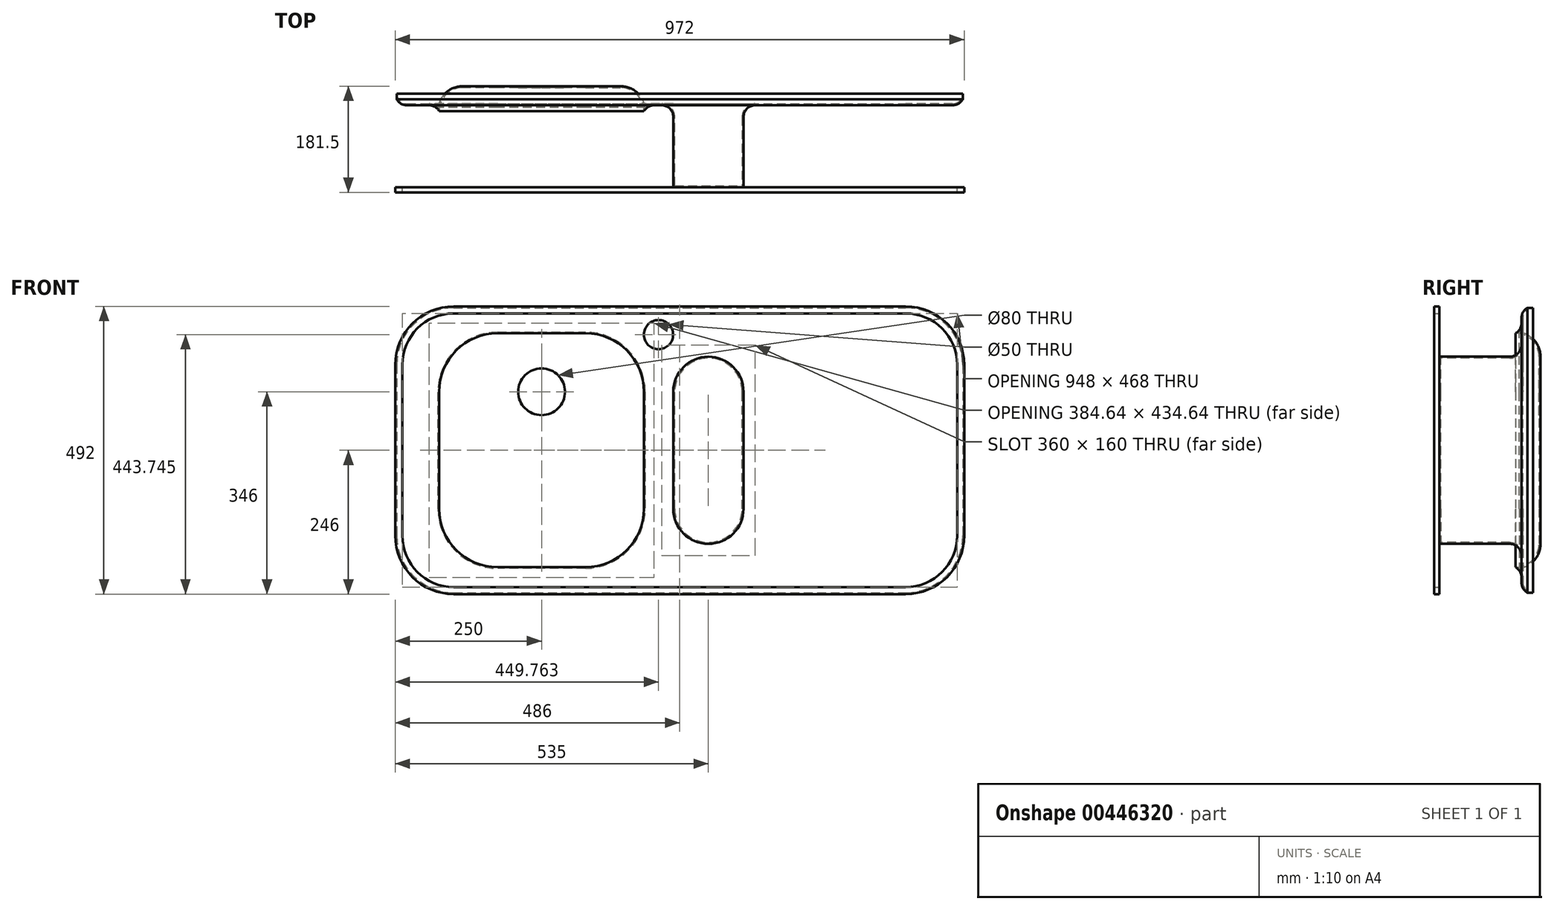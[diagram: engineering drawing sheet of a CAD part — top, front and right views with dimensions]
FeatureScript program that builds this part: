
annotation { "Feature Type Name" : "Feature", "Feature Type Description" : "" }
export const myFeature = defineFeature(function(context is Context, id is Id, definition is map)
    precondition{}
    {
        {
            var Q0;
            Q0=qCreatedBy(makeId("Front.planeOp"),FACE);
            var sketch = newSketch(context, id + "F0", { "sketchPlane" : qUnion([Q0])});
            skLineSegment(sketch, "E0.bottom", {"start": v(386, -246) * mm, "end": v(-386, -246) * mm});
            skLineSegment(sketch, "E0.top", {"start": v(386, 246) * mm, "end": v(-386, 246) * mm});
            skLineSegment(sketch, "E0.left", {"start": v(486, -146) * mm, "end": v(486, 146) * mm});
            skLineSegment(sketch, "E0.right", {"start": v(-486, -146) * mm, "end": v(-486, 146) * mm});
            skPoint(sketch, "E0.middle", {"position": v(0, 0) * mm});
            skPoint(sketch, "E1.visualSharp", {"position": v(486, -246) * mm});
            skArc(sketch, "E1.filletArc", {"start": v(386, -246) * mm, "mid": v(456.71, -216.71) * mm, "end": v(486, -146) * mm});
            skPoint(sketch, "E2.visualSharp", {"position": v(-486, -246) * mm});
            skArc(sketch, "E2.filletArc", {"start": v(-486, -146) * mm, "mid": v(-456.71, -216.71) * mm, "end": v(-386, -246) * mm});
            skPoint(sketch, "E3.visualSharp", {"position": v(-486, 246) * mm});
            skArc(sketch, "E3.filletArc", {"start": v(-386, 246) * mm, "mid": v(-456.71, 216.71) * mm, "end": v(-486, 146) * mm});
            skPoint(sketch, "E4.visualSharp", {"position": v(486, 246) * mm});
            skArc(sketch, "E4.filletArc", {"start": v(486, 146) * mm, "mid": v(456.71, 216.71) * mm, "end": v(386, 246) * mm});
            skSolve(sketch);
        }
        {
            var Q0;
            Q0 = qSketchRegion(id + "F0", true);
            extrude(context, id + "F1", {"entities" : qUnion([Q0]), "oppositeDirection" : true, "depth" : 300 * mm});
        }
        {
            var Q0;
            Q0=makeQuery(id+"F1.opExtrude","CAP_FACE",FACE,{"disambiguationData":[OSD([sQuery(id+"F0.wireOp",EDGE,"E0.bottom"),sQuery(id+"F0.wireOp",EDGE,"E0.top"),sQuery(id+"F0.wireOp",EDGE,"E0.left"),sQuery(id+"F0.wireOp",EDGE,"E0.right"),sQuery(id+"F0.wireOp",EDGE,"E1.filletArc"),sQuery(id+"F0.wireOp",EDGE,"E2.filletArc"),sQuery(id+"F0.wireOp",EDGE,"E3.filletArc"),sQuery(id+"F0.wireOp",EDGE,"E4.filletArc")])],"isStart":true});
            var sketch = newSketch(context, id + "F2", { "sketchPlane" : qUnion([Q0])});
            skLineSegment(sketch, "E5.bottom", {"start": v(-61, 200) * mm, "end": v(-411, 200) * mm});
            skLineSegment(sketch, "E5.top", {"start": v(-61, -200) * mm, "end": v(-411, -200) * mm});
            skLineSegment(sketch, "E5.left", {"start": v(-61, 200) * mm, "end": v(-61, -200) * mm});
            skLineSegment(sketch, "E5.right", {"start": v(-411, 200) * mm, "end": v(-411, -200) * mm});
            skPoint(sketch, "E5.middle", {"position": v(-236, 0) * mm});
            skSolve(sketch);
        }
        {
            var Q0;
            {var subQ5=sQuery(id+"F2.wireOp",EDGE,"E5.bottom");Q0=makeQuery(id+"F2.imprint","IMPRINT",FACE,{"disambiguationData":[TD([[makeQuery(id+"F2.imprint","IMPRINT",EDGE,{"derivedFrom":subQ5}),1.0]])]});}
            var Q1;
            {var subQ5=sQuery(id+"F2.wireOp",EDGE,"E5.top");Q1=makeQuery(id+"F2.imprint","IMPRINT",FACE,{"disambiguationData":[TD([[makeQuery(id+"F2.imprint","IMPRINT",EDGE,{"derivedFrom":subQ5}),-1.0]])]});}
            extrude(context, id + "F3", {"entities" : qUnion([Q0, Q1]), "operationType" : NewBodyOperationType.REMOVE, "oppositeDirection" : true, "depth" : 170 * mm});
        }
        {
            var Q0;
            Q0=makeQuery(id+"F3.boolean.opBoolean","COPY",FACE,{"derivedFrom":makeQuery(id+"F3.opExtrude","CAP_FACE",FACE,{"disambiguationData":[OSD([sQuery(id+"F2.wireOp",EDGE,"E5.bottom"),sQuery(id+"F2.wireOp",EDGE,"E5.top"),sQuery(id+"F2.wireOp",EDGE,"E5.left"),sQuery(id+"F2.wireOp",EDGE,"E5.right")])],"isStart":false})});
            fillet(context, id + "F4", {"entities" : qUnion([Q0]), "radius" : 40 * mm, "tangentPropagation" : true, "allowEdgeOverflow" : false});
        }
        {
            var Q0;
            Q0=makeQuery(id+"F3.boolean.opBoolean","COPY",EDGE,{"derivedFrom":makeQuery(id+"F3.opExtrude","SWEPT_EDGE",EDGE,{"disambiguationData":[OSD([sQuery(id+"F2.wireOp",EDGE,"E5.bottom"),sQuery(id+"F2.wireOp",EDGE,"E5.right")])]})});
            var Q1;
            Q1=makeQuery(id+"F3.boolean.opBoolean","COPY",EDGE,{"derivedFrom":makeQuery(id+"F3.opExtrude","SWEPT_EDGE",EDGE,{"disambiguationData":[OSD([sQuery(id+"F2.wireOp",EDGE,"E5.top"),sQuery(id+"F2.wireOp",EDGE,"E5.right")])]})});
            var Q2;
            Q2=makeQuery(id+"F3.boolean.opBoolean","COPY",EDGE,{"derivedFrom":makeQuery(id+"F3.opExtrude","SWEPT_EDGE",EDGE,{"disambiguationData":[OSD([sQuery(id+"F2.wireOp",EDGE,"E5.bottom"),sQuery(id+"F2.wireOp",EDGE,"E5.left")])]})});
            var Q3;
            Q3=makeQuery(id+"F3.boolean.opBoolean","COPY",EDGE,{"derivedFrom":makeQuery(id+"F3.opExtrude","SWEPT_EDGE",EDGE,{"disambiguationData":[OSD([sQuery(id+"F2.wireOp",EDGE,"E5.top"),sQuery(id+"F2.wireOp",EDGE,"E5.left")])]})});
            fillet(context, id + "F5", {"entities" : qUnion([Q0, Q1, Q2, Q3]), "radius" : 100 * mm, "tangentPropagation" : true, "allowEdgeOverflow" : false});
        }
        {
            var Q0;
            Q0=makeQuery(id+"F1.opExtrude","CAP_FACE",FACE,{"disambiguationData":[OSD([sQuery(id+"F0.wireOp",EDGE,"E0.bottom"),sQuery(id+"F0.wireOp",EDGE,"E0.top"),sQuery(id+"F0.wireOp",EDGE,"E0.left"),sQuery(id+"F0.wireOp",EDGE,"E0.right"),sQuery(id+"F0.wireOp",EDGE,"E1.filletArc"),sQuery(id+"F0.wireOp",EDGE,"E2.filletArc"),sQuery(id+"F0.wireOp",EDGE,"E3.filletArc"),sQuery(id+"F0.wireOp",EDGE,"E4.filletArc")])],"isStart":true});
            var sketch = newSketch(context, id + "F6", { "sketchPlane" : qUnion([Q0])});
            skArc(sketch, "E6.0.startCap", {"start": v(109, -100) * mm, "mid": v(49, -160) * mm, "end": v(-11, -100) * mm});
            skArc(sketch, "E6.0.endCap", {"start": v(-11, 100) * mm, "mid": v(49, 160) * mm, "end": v(109, 100) * mm});
            skLineSegment(sketch, "E6.0.left", {"start": v(-11, -100) * mm, "end": v(-11, 100) * mm});
            skLineSegment(sketch, "E6.0.right", {"start": v(109, -100) * mm, "end": v(109, 100) * mm});
            skSolve(sketch);
        }
        {
            var Q0;
            Q0=makeQuery(id+"F6.imprint","IMPRINT",FACE,{"disambiguationData":[TD([[makeQuery(id+"F6.imprint","IMPRINT",EDGE,{"derivedFrom":sQuery(id+"F6.wireOp",EDGE,"E6.0.startCap")}),-1.0]])]});
            extrude(context, id + "F7", {"entities" : qUnion([Q0]), "operationType" : NewBodyOperationType.REMOVE, "oppositeDirection" : true, "depth" : 140 * mm});
        }
        {
            var Q0;
            Q0=makeQuery(id+"F7.boolean.opBoolean","COPY",FACE,{"derivedFrom":makeQuery(id+"F7.opExtrude","CAP_FACE",FACE,{"disambiguationData":[OSD([sQuery(id+"F6.wireOp",EDGE,"E6.0.startCap"),sQuery(id+"F6.wireOp",EDGE,"E6.0.endCap"),sQuery(id+"F6.wireOp",EDGE,"E6.0.left"),sQuery(id+"F6.wireOp",EDGE,"E6.0.right")])],"isStart":false})});
            fillet(context, id + "F8", {"entities" : qUnion([Q0]), "radius" : 20 * mm, "tangentPropagation" : true, "allowEdgeOverflow" : false});
        }
        {
            var Q0;
            Q0=makeQuery(id+"F1.opExtrude","CAP_FACE",FACE,{"disambiguationData":[OSD([sQuery(id+"F0.wireOp",EDGE,"E0.bottom"),sQuery(id+"F0.wireOp",EDGE,"E0.top"),sQuery(id+"F0.wireOp",EDGE,"E0.left"),sQuery(id+"F0.wireOp",EDGE,"E0.right"),sQuery(id+"F0.wireOp",EDGE,"E1.filletArc"),sQuery(id+"F0.wireOp",EDGE,"E2.filletArc"),sQuery(id+"F0.wireOp",EDGE,"E3.filletArc"),sQuery(id+"F0.wireOp",EDGE,"E4.filletArc")])],"isStart":true});
            var sketch = newSketch(context, id + "F9", { "sketchPlane" : qUnion([Q0])});
            skArc(sketch, "E7.0", {"start": v(-386, 246) * mm, "mid": v(-456.71, 216.71) * mm, "end": v(-486, 146) * mm});
            skArc(sketch, "E7.1", {"start": v(-486, -146) * mm, "mid": v(-456.71, -216.71) * mm, "end": v(-386, -246) * mm});
            skLineSegment(sketch, "E7.2", {"start": v(386, 246) * mm, "end": v(-386, 246) * mm});
            skArc(sketch, "E7.3", {"start": v(386, -246) * mm, "mid": v(456.71, -216.71) * mm, "end": v(486, -146) * mm});
            skLineSegment(sketch, "E7.4", {"start": v(-486, -146) * mm, "end": v(-486, 146) * mm});
            skArc(sketch, "E7.5", {"start": v(486, 146) * mm, "mid": v(456.71, 216.71) * mm, "end": v(386, 246) * mm});
            skLineSegment(sketch, "E7.6", {"start": v(486, -146) * mm, "end": v(486, 146) * mm});
            skLineSegment(sketch, "E7.7", {"start": v(386, -246) * mm, "end": v(-386, -246) * mm});
            skArc(sketch, "E8.0", {"start": v(474, 146) * mm, "mid": v(448.23, 208.23) * mm, "end": v(386, 234) * mm});
            skLineSegment(sketch, "E8.1", {"start": v(474, -146) * mm, "end": v(474, 146) * mm});
            skLineSegment(sketch, "E8.2", {"start": v(386, 234) * mm, "end": v(-386, 234) * mm});
            skArc(sketch, "E8.3", {"start": v(386, -234) * mm, "mid": v(448.23, -208.23) * mm, "end": v(474, -146) * mm});
            skArc(sketch, "E8.4", {"start": v(-386, 234) * mm, "mid": v(-448.23, 208.23) * mm, "end": v(-474, 146) * mm});
            skLineSegment(sketch, "E8.5", {"start": v(-474, -146) * mm, "end": v(-474, 146) * mm});
            skArc(sketch, "E8.6", {"start": v(-474, -146) * mm, "mid": v(-448.23, -208.23) * mm, "end": v(-386, -234) * mm});
            skLineSegment(sketch, "E8.7", {"start": v(386, -234) * mm, "end": v(-386, -234) * mm});
            skSolve(sketch);
        }
        {
            var Q0;
            Q0 = qSketchRegion(id + "F9", true);
            extrude(context, id + "F10", {"entities" : qUnion([Q0]), "operationType" : NewBodyOperationType.ADD, "depth" : 9 * mm});
        }
        {
            var Q0;
            Q0=makeQuery(id+"F1.opExtrude","CAP_FACE",FACE,{"disambiguationData":[OSD([sQuery(id+"F0.wireOp",EDGE,"E0.bottom"),sQuery(id+"F0.wireOp",EDGE,"E0.top"),sQuery(id+"F0.wireOp",EDGE,"E0.left"),sQuery(id+"F0.wireOp",EDGE,"E0.right"),sQuery(id+"F0.wireOp",EDGE,"E1.filletArc"),sQuery(id+"F0.wireOp",EDGE,"E2.filletArc"),sQuery(id+"F0.wireOp",EDGE,"E3.filletArc"),sQuery(id+"F0.wireOp",EDGE,"E4.filletArc")])],"isStart":false});
            shell(context, id + "F11", {"entities" : qUnion([Q0]), "thickness" : 2.5 * mm});
        }
        {
            var Q0;
            Q0=makeQuery(id+"F1.opExtrude","CAP_FACE",FACE,{"disambiguationData":[OSD([sQuery(id+"F0.wireOp",EDGE,"E0.bottom"),sQuery(id+"F0.wireOp",EDGE,"E0.top"),sQuery(id+"F0.wireOp",EDGE,"E0.left"),sQuery(id+"F0.wireOp",EDGE,"E0.right"),sQuery(id+"F0.wireOp",EDGE,"E1.filletArc"),sQuery(id+"F0.wireOp",EDGE,"E2.filletArc"),sQuery(id+"F0.wireOp",EDGE,"E3.filletArc"),sQuery(id+"F0.wireOp",EDGE,"E4.filletArc")])],"isStart":false});
            extrude(context, id + "F12", {"entities" : qUnion([Q0]), "operationType" : NewBodyOperationType.REMOVE, "oppositeDirection" : true, "depth" : 267.66 * mm});
        }
        {
            var Q0;
            Q0=makeQuery(id+"F3.boolean.opBoolean","COPY",FACE,{"derivedFrom":makeQuery(id+"F3.opExtrude","CAP_FACE",FACE,{"disambiguationData":[OSD([sQuery(id+"F2.wireOp",EDGE,"E5.bottom"),sQuery(id+"F2.wireOp",EDGE,"E5.top"),sQuery(id+"F2.wireOp",EDGE,"E5.left"),sQuery(id+"F2.wireOp",EDGE,"E5.right")])],"isStart":false})});
            var sketch = newSketch(context, id + "F13", { "sketchPlane" : qUnion([Q0])});
            skCircle(sketch, "E9", {"center": v(-236, 100) * mm, "radius": 40 * mm});
            skPoint(sketch, "E9.centerSnap0", {"position": v(-236, 160) * mm});
            skSolve(sketch);
        }
        {
            var Q0;
            Q0 = qSketchRegion(id + "F13", true);
            extrude(context, id + "F14", {"entities" : qUnion([Q0]), "operationType" : NewBodyOperationType.REMOVE, "endBound" : BoundingType.THROUGH_ALL, "oppositeDirection" : true, "depth" : 25 * mm});
        }
        {
            var Q0;
            Q0=makeQuery(id+"F7.boolean.opBoolean","COPY",FACE,{"derivedFrom":makeQuery(id+"F7.opExtrude","CAP_FACE",FACE,{"disambiguationData":[OSD([sQuery(id+"F6.wireOp",EDGE,"E6.0.startCap"),sQuery(id+"F6.wireOp",EDGE,"E6.0.endCap"),sQuery(id+"F6.wireOp",EDGE,"E6.0.left"),sQuery(id+"F6.wireOp",EDGE,"E6.0.right")])],"isStart":false})});
            var sketch = newSketch(context, id + "F15", { "sketchPlane" : qUnion([Q0])});
            skCircle(sketch, "E10", {"center": v(49, 100) * mm, "radius": 25 * mm});
            skSolve(sketch);
        }
        {
            var Q0;
            Q0 = qSketchRegion(id + "F15", true);
            extrude(context, id + "F16", {"entities" : qUnion([Q0]), "operationType" : NewBodyOperationType.REMOVE, "endBound" : BoundingType.THROUGH_ALL, "oppositeDirection" : true, "depth" : 25 * mm});
        }
        {
            var Q0;
            Q0=makeQuery(id+"F1.opExtrude","CAP_FACE",FACE,{"disambiguationData":[OSD([sQuery(id+"F0.wireOp",EDGE,"E0.bottom"),sQuery(id+"F0.wireOp",EDGE,"E0.top"),sQuery(id+"F0.wireOp",EDGE,"E0.left"),sQuery(id+"F0.wireOp",EDGE,"E0.right"),sQuery(id+"F0.wireOp",EDGE,"E1.filletArc"),sQuery(id+"F0.wireOp",EDGE,"E2.filletArc"),sQuery(id+"F0.wireOp",EDGE,"E3.filletArc"),sQuery(id+"F0.wireOp",EDGE,"E4.filletArc")])],"isStart":true});
            var sketch = newSketch(context, id + "F17", { "sketchPlane" : qUnion([Q0])});
            skCircle(sketch, "E11", {"center": v(-36.24, 197.74) * mm, "radius": 25 * mm});
            skSolve(sketch);
        }
        {
            var Q0;
            Q0 = qSketchRegion(id + "F17", true);
            extrude(context, id + "F18", {"entities" : qUnion([Q0]), "operationType" : NewBodyOperationType.REMOVE, "endBound" : BoundingType.THROUGH_ALL, "oppositeDirection" : true, "depth" : 25 * mm});
        }
    });
